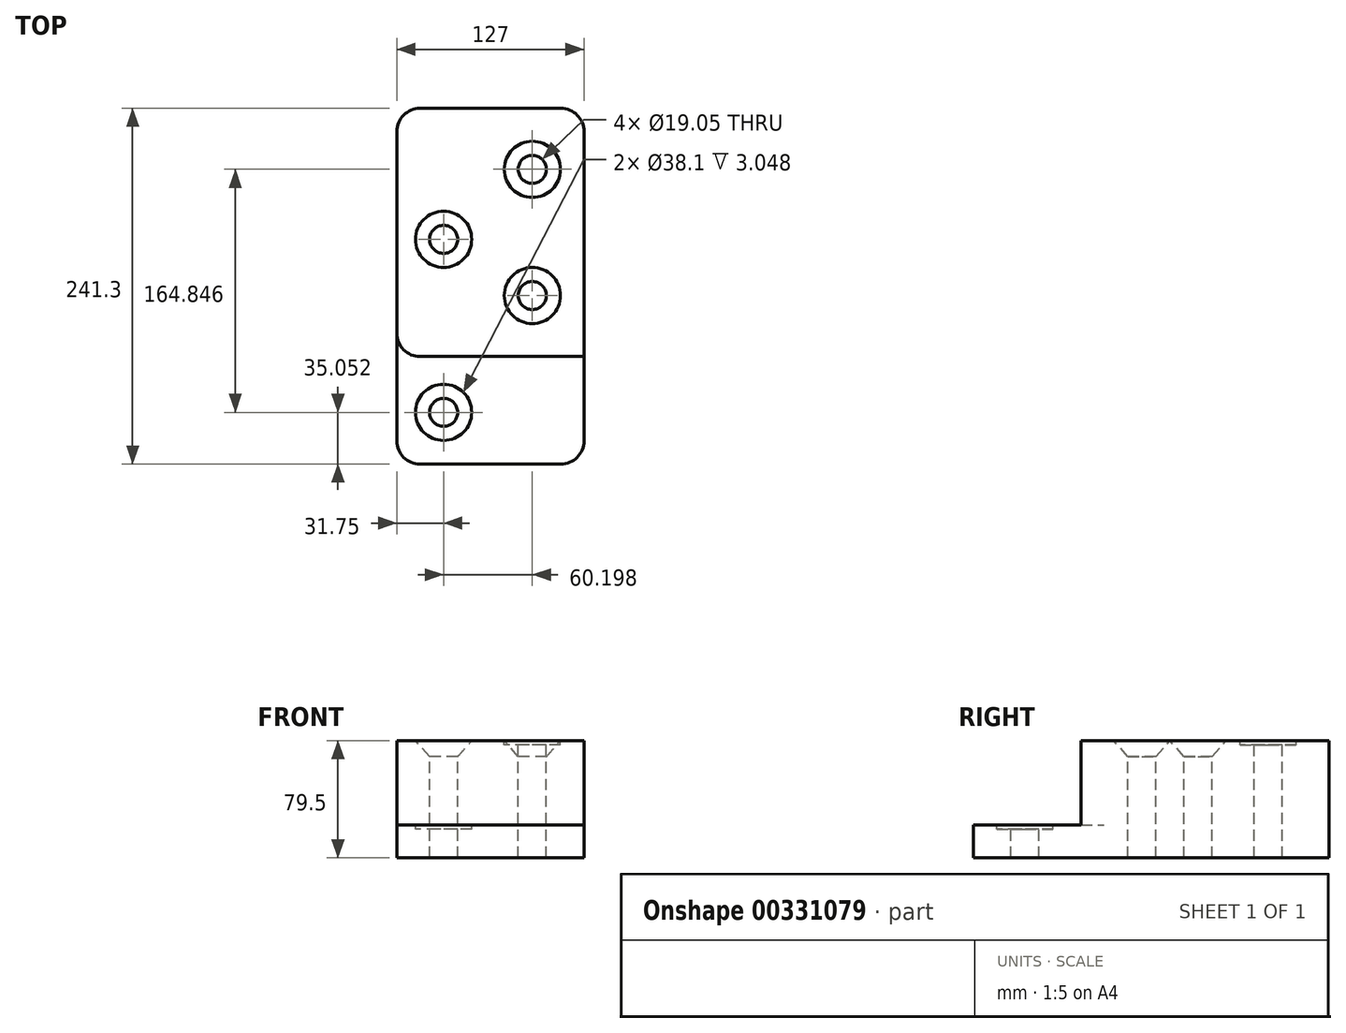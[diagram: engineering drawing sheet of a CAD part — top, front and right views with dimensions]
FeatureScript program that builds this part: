
annotation { "Feature Type Name" : "Feature", "Feature Type Description" : "" }
export const myFeature = defineFeature(function(context is Context, id is Id, definition is map)
    precondition{}
    {
        {
            var Q0;
            Q0=qCreatedBy(makeId("Front.planeOp"),FACE);
            var sketch = newSketch(context, id + "F0", { "sketchPlane" : qUnion([Q0])});
            skLineSegment(sketch, "E0.bottom", {"start": v(-63.5, 0) * mm, "end": v(63.5, 0) * mm});
            skLineSegment(sketch, "E0.top", {"start": v(-63.5, 79.5) * mm, "end": v(63.5, 79.5) * mm});
            skLineSegment(sketch, "E0.left", {"start": v(-63.5, 0) * mm, "end": v(-63.5, 79.5) * mm});
            skLineSegment(sketch, "E0.right", {"start": v(63.5, 0) * mm, "end": v(63.5, 79.5) * mm});
            skSolve(sketch);
        }
        {
            var Q0;
            Q0 = qSketchRegion(id + "F0", true);
            extrude(context, id + "F1", {"entities" : qUnion([Q0]), "endBound" : BoundingType.SYMMETRIC, "oppositeDirection" : true, "depth" : 241.3 * mm});
        }
        {
            var Q0;
            Q0=makeQuery(id+"F1.opExtrude","SWEPT_FACE",FACE,{"disambiguationData":[OSD([sQuery(id+"F0.wireOp",EDGE,"E0.right")])]});
            var sketch = newSketch(context, id + "F2", { "sketchPlane" : qUnion([Q0])});
            skLineSegment(sketch, "E1.0.0", {"start": v(-120.65, 79.5) * mm, "end": v(-120.65, 22.35) * mm});
            skLineSegment(sketch, "E1.0.3", {"start": v(-47.75, 79.5) * mm, "end": v(-120.65, 79.5) * mm});
            skLineSegment(sketch, "E2.bottom", {"start": v(-120.65, 79.5) * mm, "end": v(-47.75, 79.5) * mm});
            skLineSegment(sketch, "E2.top", {"start": v(-120.65, 22.35) * mm, "end": v(-47.75, 22.35) * mm});
            skLineSegment(sketch, "E2.right", {"start": v(-47.75, 79.5) * mm, "end": v(-47.75, 22.35) * mm});
            skPoint(sketch, "E1.0.1.start.orphan", {"position": v(-120.65, 0) * mm});
            skPoint(sketch, "E1.0.2.end.orphan", {"position": v(120.65, 79.5) * mm});
            skPoint(sketch, "E1.0.2.start.orphan", {"position": v(120.65, 0) * mm});
            skSolve(sketch);
        }
        {
            var Q0;
            Q0 = qSketchRegion(id + "F2", true);
            extrude(context, id + "F3", {"entities" : qUnion([Q0]), "operationType" : NewBodyOperationType.REMOVE, "endBound" : BoundingType.THROUGH_ALL, "oppositeDirection" : true, "depth" : 25.4 * mm});
        }
        {
            var Q0;
            Q0=makeQuery(id+"F3.boolean.opBoolean","COPY",FACE,{"derivedFrom":makeQuery(id+"F3.opExtrude","SWEPT_FACE",FACE,{"disambiguationData":[OSD([sQuery(id+"F2.wireOp",EDGE,"E2.top")])]})});
            var sketch = newSketch(context, id + "F4", { "sketchPlane" : qUnion([Q0])});
            skPoint(sketch, "E3", {"position": v(-31.75, -85.6) * mm});
            skSolve(sketch);
        }
        {
            var Q0;
            Q0=makeQuery(id+"F1.opExtrude","SWEPT_FACE",FACE,{"disambiguationData":[OSD([sQuery(id+"F0.wireOp",EDGE,"E0.top")])]});
            var sketch = newSketch(context, id + "F5", { "sketchPlane" : qUnion([Q0])});
            skPoint(sketch, "E4", {"position": v(-31.75, 31.75) * mm});
            skPoint(sketch, "E5", {"position": v(28.45, -6.35) * mm});
            skPoint(sketch, "E6", {"position": v(28.45, 79.25) * mm});
            skSolve(sketch);
        }
        {
            var Q0;
            Q0=sQuery(id+"F5.wireOp",VERTEX,"E6");
            var Q1;
            Q1=sQuery(id+"F4.wireOp",VERTEX,"E3");
            var Q2;
            Q2=makeQuery(id+"F1.opExtrude","SWEPT_BODY",BODY,{"disambiguationData":[OSD([sQuery(id+"F0.wireOp",EDGE,"E0.bottom"),sQuery(id+"F0.wireOp",EDGE,"E0.top"),sQuery(id+"F0.wireOp",EDGE,"E0.left"),sQuery(id+"F0.wireOp",EDGE,"E0.right")])]});
            hole(context, id + "F6", {"style" : HoleStyle.C_BORE, "endStyle" : HoleEndStyle.THROUGH, "holeDiameter" : 19.05 * mm, "cBoreDiameter" : 38.1 * mm, "cBoreDepth" : 3.05 * mm, "tappedDepth" : 12.7 * mm, "tapClearance" : 3, "locations" : qUnion([Q0, Q1]), "scope" : qUnion([Q2])});
        }
        {
            var Q0;
            Q0=sQuery(id+"F5.wireOp",VERTEX,"E4");
            var Q1;
            Q1=sQuery(id+"F5.wireOp",VERTEX,"E5");
            var Q2;
            Q2=makeQuery(id+"F1.opExtrude","SWEPT_BODY",BODY,{"disambiguationData":[OSD([sQuery(id+"F0.wireOp",EDGE,"E0.bottom"),sQuery(id+"F0.wireOp",EDGE,"E0.top"),sQuery(id+"F0.wireOp",EDGE,"E0.left"),sQuery(id+"F0.wireOp",EDGE,"E0.right")])]});
            hole(context, id + "F7", {"style" : HoleStyle.C_SINK, "endStyle" : HoleEndStyle.THROUGH, "holeDiameter" : 19.05 * mm, "cSinkDiameter" : 38.1 * mm, "cSinkAngle" : 82 * degree, "tappedDepth" : 12.7 * mm, "tapClearance" : 3, "locations" : qUnion([Q0, Q1]), "scope" : qUnion([Q2])});
        }
        {
            var Q0;
            Q0=makeQuery(id+"F3.boolean.opBoolean","INTERSECT",EDGE,{"derivedFrom":[makeQuery(id+"F1.opExtrude","SWEPT_FACE",FACE,{"disambiguationData":[OSD([sQuery(id+"F0.wireOp",EDGE,"E0.left")])]}),makeQuery(id+"F3.opExtrude","SWEPT_FACE",FACE,{"disambiguationData":[OSD([sQuery(id+"F2.wireOp",EDGE,"E2.right")])]})]});
            var Q1;
            Q1=makeQuery(id+"F3.boolean.opBoolean","COPY",EDGE,{"derivedFrom":makeQuery(id+"F3.opExtrude","CAP_EDGE",EDGE,{"disambiguationData":[OSD([sQuery(id+"F2.wireOp",EDGE,"E2.right")])],"isStart":true})});
            var Q2;
            Q2=makeQuery(id+"F1.opExtrude","CAP_EDGE",EDGE,{"disambiguationData":[OSD([sQuery(id+"F0.wireOp",EDGE,"E0.right")])],"isStart":true});
            var Q3;
            Q3=makeQuery(id+"F1.opExtrude","CAP_EDGE",EDGE,{"disambiguationData":[OSD([sQuery(id+"F0.wireOp",EDGE,"E0.left")])],"isStart":true});
            var Q4;
            Q4=makeQuery(id+"F1.opExtrude","CAP_EDGE",EDGE,{"disambiguationData":[OSD([sQuery(id+"F0.wireOp",EDGE,"E0.right")])],"isStart":false});
            var Q5;
            Q5=makeQuery(id+"F1.opExtrude","CAP_EDGE",EDGE,{"disambiguationData":[OSD([sQuery(id+"F0.wireOp",EDGE,"E0.left")])],"isStart":false});
            fillet(context, id + "F8", {"entities" : qUnion([Q0, Q1, Q2, Q3, Q4, Q5]), "radius" : 15.75 * mm, "tangentPropagation" : true, "allowEdgeOverflow" : false});
        }
    });
